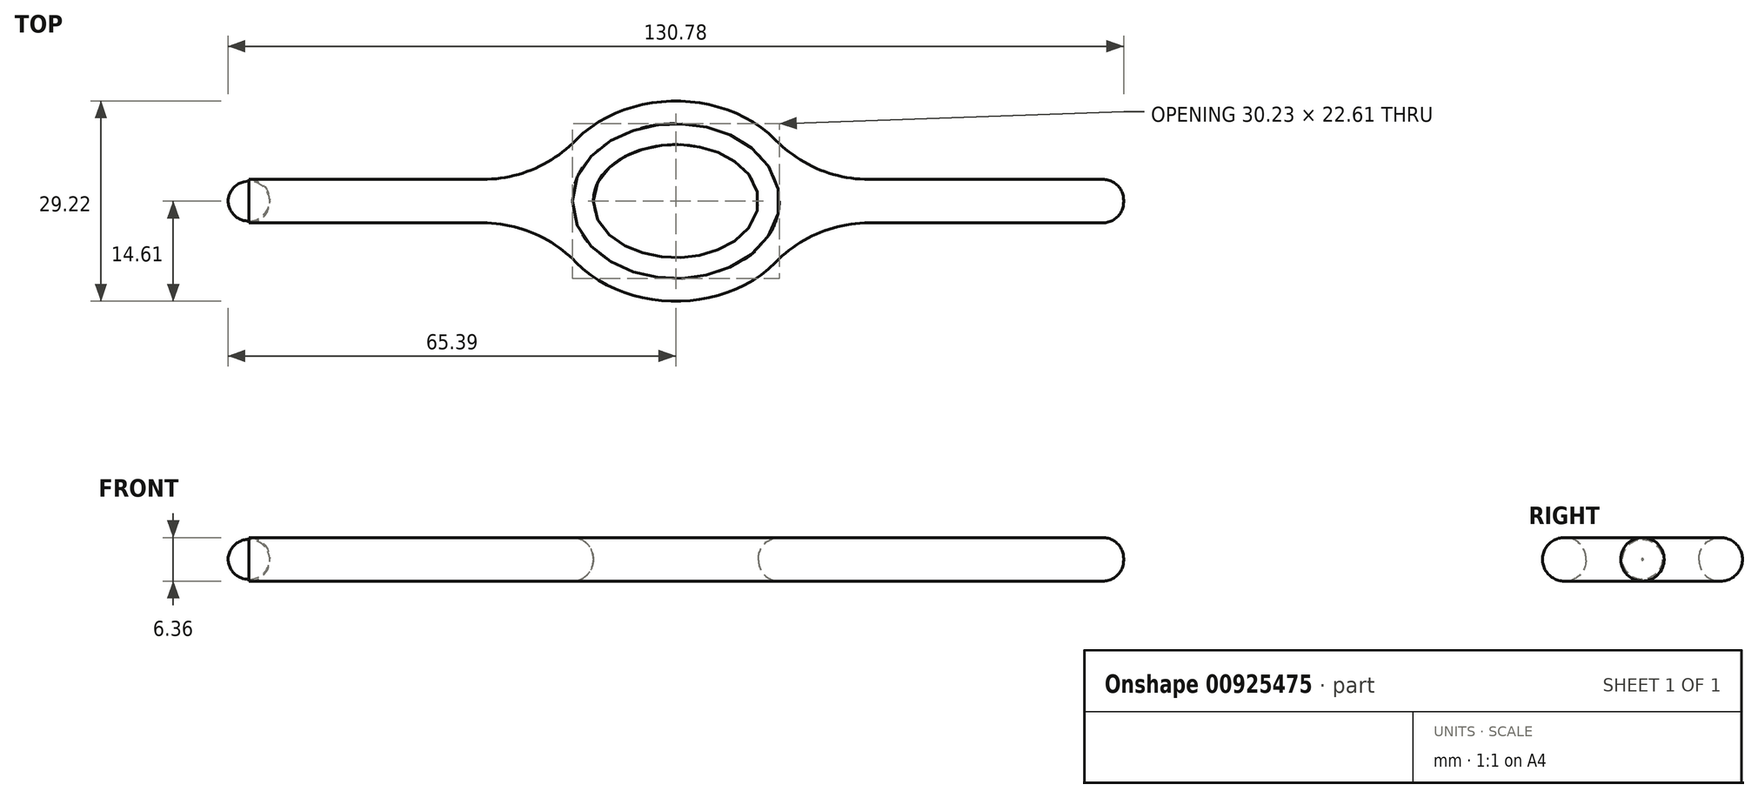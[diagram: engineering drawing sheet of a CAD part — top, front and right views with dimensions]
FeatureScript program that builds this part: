
annotation { "Feature Type Name" : "Feature", "Feature Type Description" : "" }
export const myFeature = defineFeature(function(context is Context, id is Id, definition is map)
    precondition{}
    {
        {
            var Q0;
            Q0=qCreatedBy(makeId("Top.planeOp"),FACE);
            var sketch = newSketch(context, id + "F0", { "sketchPlane" : qUnion([Q0])});
            skLineSegment(sketch, "E0.bottom", {"start": v(65.4, 3.18) * mm, "end": v(28.22, 3.18) * mm});
            skLineSegment(sketch, "E0.top", {"start": v(65.4, -3.18) * mm, "end": v(28.22, -3.18) * mm});
            skLineSegment(sketch, "E0.left", {"start": v(65.4, 3.18) * mm, "end": v(65.4, -3.18) * mm});
            skLineSegment(sketch, "E0.right", {"start": v(-65.4, 3.18) * mm, "end": v(-65.4, -3.18) * mm});
            skPoint(sketch, "E0.middle", {"position": v(0, 0) * mm});
            skEllipticalArc(sketch, "E1", {});
            skEllipse(sketch, "E2", {"center": v(0, 0) * mm, "majorRadius": 12.07 * mm, "minorRadius": 8.26 * mm, "majorAxis": v(-1, 0)});
            skLineSegment(sketch, "E3.trimOffspring", {"start": v(-28.22, 3.18) * mm, "end": v(-65.4, 3.18) * mm});
            skLineSegment(sketch, "E4.trimOffspring", {"start": v(-28.22, -3.18) * mm, "end": v(-65.4, -3.18) * mm});
            skEllipticalArc(sketch, "E5.trimOffspring", {});
            skPoint(sketch, "E6.visualSharp", {"position": v(-17.97, 3.18) * mm});
            skArc(sketch, "E6.filletArc", {"start": v(-28.22, 3.18) * mm, "mid": v(-20.81, 4.67) * mm, "end": v(-14.57, 8.93) * mm});
            skPoint(sketch, "E7.visualSharp", {"position": v(-17.97, -3.17) * mm});
            skArc(sketch, "E7.filletArc", {"start": v(-14.57, -8.93) * mm, "mid": v(-20.81, -4.67) * mm, "end": v(-28.22, -3.18) * mm});
            skPoint(sketch, "E8.visualSharp", {"position": v(17.97, 3.18) * mm});
            skArc(sketch, "E8.filletArc", {"start": v(14.57, 8.93) * mm, "mid": v(20.81, 4.67) * mm, "end": v(28.22, 3.18) * mm});
            skPoint(sketch, "E9.visualSharp", {"position": v(17.97, -3.18) * mm});
            skArc(sketch, "E9.filletArc", {"start": v(28.22, -3.18) * mm, "mid": v(20.81, -4.67) * mm, "end": v(14.57, -8.93) * mm});
            const initialGuessF0  = {"E1": [0, 0, 1, 0, 0.018415, 0.014605, 3.7995140395410694, 5.62526392122831], "E5.trimOffspring": [0, 0, 1, 0, 0.018415, 0.014605, 0.6579213859512766, 2.483671267638517]};
            skSetInitialGuess(sketch, initialGuessF0);
            skSolve(sketch);
        }
        {
            var Q0;
            Q0 = qSketchRegion(id + "F0", true);
            extrude(context, id + "F1", {"entities" : qUnion([Q0]), "endBound" : BoundingType.SYMMETRIC, "depth" : 6.35 * mm, "offsetDistance" : 25.4 * mm});
        }
        {
            var Q0;
            Q0=makeQuery(id+"F1.opExtrude","CAP_EDGE",EDGE,{"disambiguationData":[OSD([sQuery(id+"F0.wireOp",EDGE,"E4.trimOffspring")])],"isStart":false});
            var Q1;
            Q1=makeQuery(id+"F1.opExtrude","CAP_EDGE",EDGE,{"disambiguationData":[OSD([sQuery(id+"F0.wireOp",EDGE,"E4.trimOffspring")])],"isStart":true});
            var Q2;
            Q2=makeQuery(id+"F1.opExtrude","CAP_EDGE",EDGE,{"disambiguationData":[OSD([sQuery(id+"F0.wireOp",EDGE,"E3.trimOffspring")])],"isStart":false});
            var Q3;
            Q3=makeQuery(id+"F1.opExtrude","CAP_EDGE",EDGE,{"disambiguationData":[OSD([sQuery(id+"F0.wireOp",EDGE,"E3.trimOffspring")])],"isStart":true});
            fillet(context, id + "F2", {"entities" : qUnion([Q0, Q1, Q2, Q3]), "radius" : 3.17 * mm, "tangentPropagation" : true, "allowEdgeOverflow" : false});
        }
        {
            var Q0;
            Q0=makeQuery(id+"F2.opFillet","BLEND_EDGE",EDGE,{"blendedFrom":[makeQuery(id+"F1.opExtrude","CAP_EDGE",EDGE,{"disambiguationData":[OSD([sQuery(id+"F0.wireOp",EDGE,"E0.bottom")])],"isStart":true}),makeQuery(id+"F1.opExtrude","SWEPT_FACE",FACE,{"disambiguationData":[OSD([sQuery(id+"F0.wireOp",EDGE,"E0.left")])]})],"blendedInto":[makeQuery(id+"F1.opExtrude","SWEPT_FACE",FACE,{"disambiguationData":[OSD([sQuery(id+"F0.wireOp",EDGE,"E0.left")])]})]});
            fillet(context, id + "F3", {"entities" : qUnion([Q0]), "radius" : 3.05 * mm, "tangentPropagation" : true, "allowEdgeOverflow" : false});
        }
        {
            var Q0;
            Q0=makeQuery(id+"F2.opFillet","BLEND_EDGE",EDGE,{"blendedFrom":[makeQuery(id+"F1.opExtrude","CAP_EDGE",EDGE,{"disambiguationData":[OSD([sQuery(id+"F0.wireOp",EDGE,"E3.trimOffspring")])],"isStart":true}),makeQuery(id+"F1.opExtrude","SWEPT_FACE",FACE,{"disambiguationData":[OSD([sQuery(id+"F0.wireOp",EDGE,"E0.right")])]})],"blendedInto":[makeQuery(id+"F1.opExtrude","SWEPT_FACE",FACE,{"disambiguationData":[OSD([sQuery(id+"F0.wireOp",EDGE,"E0.right")])]})]});
            fillet(context, id + "F4", {"entities" : qUnion([Q0]), "radius" : 3.05 * mm, "tangentPropagation" : true, "allowEdgeOverflow" : false});
        }
        {
            var Q0;
            Q0=makeQuery(id+"F1.opExtrude","CAP_EDGE",EDGE,{"disambiguationData":[OSD([sQuery(id+"F0.wireOp",EDGE,"E2")])],"isStart":false});
            var Q1;
            Q1=makeQuery(id+"F1.opExtrude","CAP_EDGE",EDGE,{"disambiguationData":[OSD([sQuery(id+"F0.wireOp",EDGE,"E2")])],"isStart":true});
            fillet(context, id + "F5", {"entities" : qUnion([Q0, Q1]), "radius" : 3.05 * mm, "tangentPropagation" : true, "allowEdgeOverflow" : false});
        }
    });
